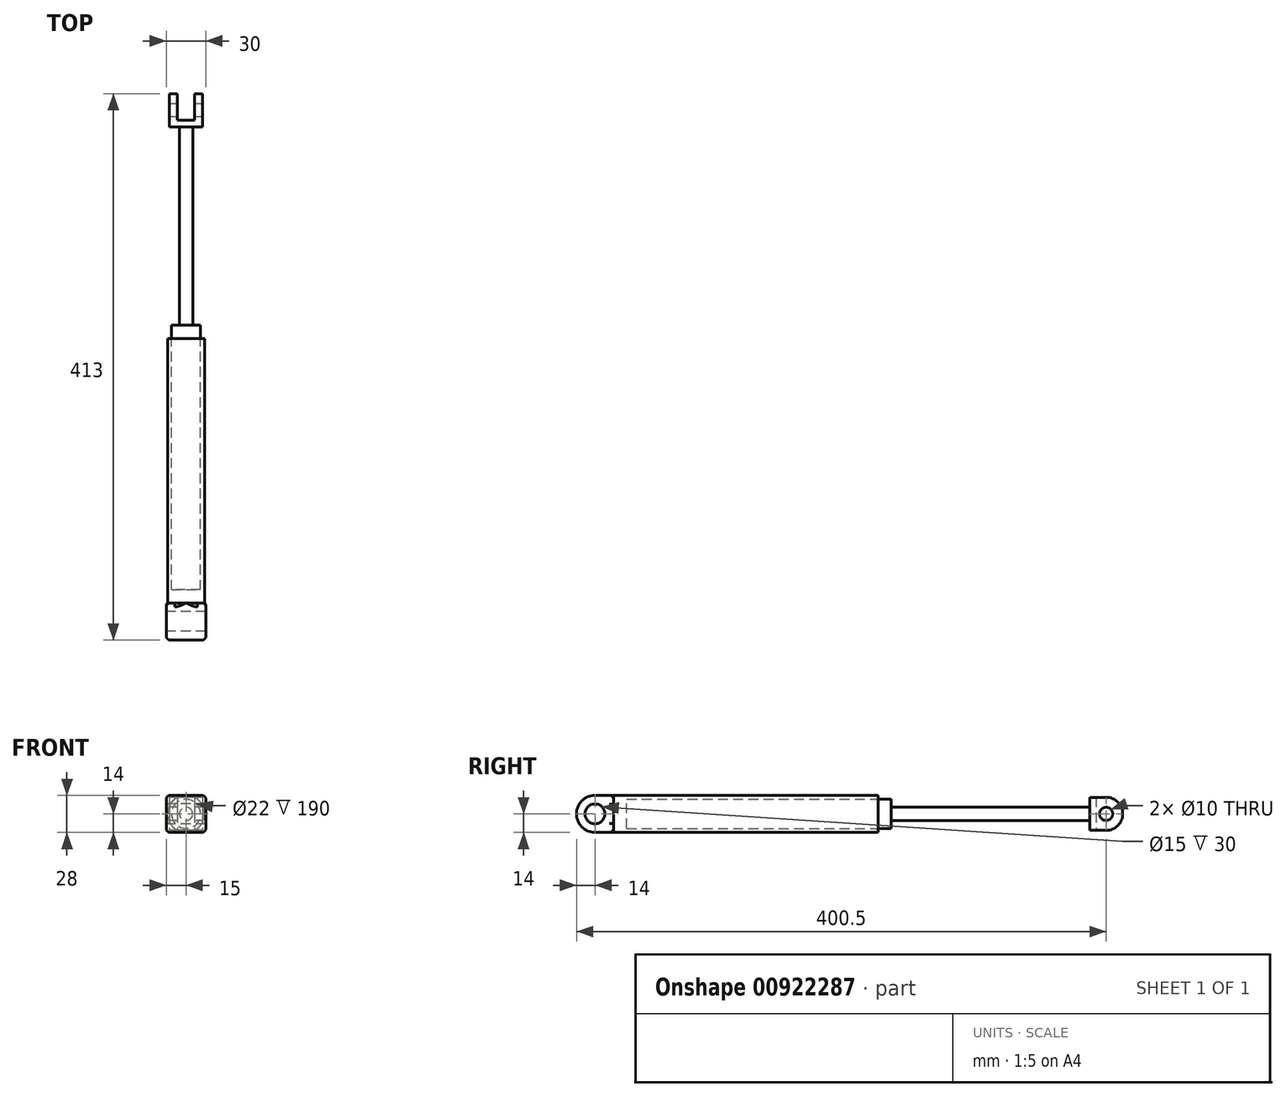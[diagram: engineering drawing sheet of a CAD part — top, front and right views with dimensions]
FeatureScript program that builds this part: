
annotation { "Feature Type Name" : "Feature", "Feature Type Description" : "" }
export const myFeature = defineFeature(function(context is Context, id is Id, definition is map)
    precondition{}
    {
        {
            var Q0;
            Q0=qCreatedBy(makeId("Front.planeOp"),FACE);
            var sketch = newSketch(context, id + "F0", { "sketchPlane" : qUnion([Q0])});
            skCircle(sketch, "E0", {"center": v(0, 0) * mm, "radius": 14 * mm});
            skCircle(sketch, "E1", {"center": v(0, 0) * mm, "radius": 11 * mm});
            skSolve(sketch);
        }
        {
            var Q0;
            Q0=makeQuery(id+"F0.imprint","IMPRINT",FACE,{"disambiguationData":[TD([[makeQuery(id+"F0.imprint","IMPRINT",EDGE,{"derivedFrom":sQuery(id+"F0.wireOp",EDGE,"E0")}),1.0]])]});
            var Q1;
            Q1=makeQuery(id+"F0.imprint","IMPRINT",FACE,{"disambiguationData":[TD([[makeQuery(id+"F0.imprint","IMPRINT",EDGE,{"derivedFrom":sQuery(id+"F0.wireOp",EDGE,"E1")}),1.0]])]});
            extrude(context, id + "F1", {"entities" : qUnion([Q0, Q1]), "depth" : 200 * mm, "offsetDistance" : 25 * mm});
        }
        {
            var Q0;
            Q0=makeQuery(id+"F0.imprint","IMPRINT",FACE,{"disambiguationData":[TD([[makeQuery(id+"F0.imprint","IMPRINT",EDGE,{"derivedFrom":sQuery(id+"F0.wireOp",EDGE,"E1")}),1.0]])]});
            extrude(context, id + "F2", {"entities" : qUnion([Q0]), "operationType" : NewBodyOperationType.REMOVE, "depth" : 190 * mm, "offsetDistance" : 25 * mm});
        }
        {
            var Q0;
            Q0=qCreatedBy(makeId("Right.planeOp"),FACE);
            var sketch = newSketch(context, id + "F3", { "sketchPlane" : qUnion([Q0])});
            skLineSegment(sketch, "E2.bottom", {"start": v(-200, 14) * mm, "end": v(-214, 14) * mm});
            skLineSegment(sketch, "E2.top", {"start": v(-200, -14) * mm, "end": v(-214, -14) * mm});
            skLineSegment(sketch, "E2.left", {"start": v(-200, 14) * mm, "end": v(-200, -14) * mm});
            skLineSegment(sketch, "E2.right", {"start": v(-228, 0) * mm, "end": v(-228, 0) * mm});
            skPoint(sketch, "E3.visualSharp", {"position": v(-228, 14) * mm});
            skArc(sketch, "E3.filletArc", {"start": v(-214, 14) * mm, "mid": v(-223.9, 9.9) * mm, "end": v(-228, 0) * mm});
            skPoint(sketch, "E4.visualSharp", {"position": v(-228, -14) * mm});
            skArc(sketch, "E4.filletArc", {"start": v(-228, 0) * mm, "mid": v(-223.9, -9.9) * mm, "end": v(-214, -14) * mm});
            skCircle(sketch, "E5", {"center": v(-214, 0) * mm, "radius": 7.5 * mm});
            skSolve(sketch);
        }
        {
            var Q0;
            Q0 = qSketchRegion(id + "F3", true);
            extrude(context, id + "F4", {"entities" : qUnion([Q0]), "operationType" : NewBodyOperationType.ADD, "depth" : 30 * mm, "offsetDistance" : 25 * mm, "symmetric" : true});
        }
        {
            var Q0;
            Q0=makeQuery(id+"F4.opExtrude","CAP_EDGE",EDGE,{"disambiguationData":[OSD([sQuery(id+"F3.wireOp",EDGE,"E2.bottom")])],"isStart":true});
            var Q1;
            Q1=makeQuery(id+"F4.opExtrude","CAP_EDGE",EDGE,{"disambiguationData":[OSD([sQuery(id+"F3.wireOp",EDGE,"E2.bottom")])],"isStart":false});
            var Q2;
            Q2=makeQuery(id+"F4.opExtrude","CAP_EDGE",EDGE,{"disambiguationData":[OSD([sQuery(id+"F3.wireOp",EDGE,"E2.left")])],"isStart":false});
            var Q3;
            {var subQ0=sQuery(id+"F3.wireOp",EDGE,"E2.bottom");var subQ1=sQuery(id+"F3.wireOp",EDGE,"E2.left");Q3=makeQuery(id+"F4.boolean.opBoolean","SPLIT",EDGE,{"disambiguationData":[TD([makeQuery(id+"F4.opExtrude","CAP_FACE",FACE,{"disambiguationData":[OSD([subQ0,sQuery(id+"F3.wireOp",EDGE,"E2.top"),subQ1,sQuery(id+"F3.wireOp",EDGE,"E3.filletArc"),sQuery(id+"F3.wireOp",EDGE,"E4.filletArc"),sQuery(id+"F3.wireOp",EDGE,"E5")])],"isStart":false})])],"derivedFrom":makeQuery(id+"F4.opExtrude","SWEPT_EDGE",EDGE,{"disambiguationData":[OSD([subQ0,subQ1])]})});}
            var Q4;
            Q4=makeQuery(id+"F4.opExtrude","CAP_EDGE",EDGE,{"disambiguationData":[OSD([sQuery(id+"F3.wireOp",EDGE,"E2.left")])],"isStart":true});
            var Q5;
            {var subQ0=sQuery(id+"F3.wireOp",EDGE,"E2.left");var subQ1=sQuery(id+"F3.wireOp",EDGE,"E2.top");Q5=makeQuery(id+"F4.boolean.opBoolean","SPLIT",EDGE,{"disambiguationData":[TD([makeQuery(id+"F4.opExtrude","CAP_FACE",FACE,{"disambiguationData":[OSD([sQuery(id+"F3.wireOp",EDGE,"E2.bottom"),subQ1,subQ0,sQuery(id+"F3.wireOp",EDGE,"E3.filletArc"),sQuery(id+"F3.wireOp",EDGE,"E4.filletArc"),sQuery(id+"F3.wireOp",EDGE,"E5")])],"isStart":true})])],"derivedFrom":makeQuery(id+"F4.opExtrude","SWEPT_EDGE",EDGE,{"disambiguationData":[OSD([subQ1,subQ0])]})});}
            fillet(context, id + "F5", {"entities" : qUnion([Q0, Q1, Q2, Q3, Q4, Q5]), "radius" : 3 * mm, "tangentPropagation" : true, "allowEdgeOverflow" : false});
        }
        {
            var Q0;
            Q0=qCreatedBy(makeId("Front.planeOp"),FACE);
            var sketch = newSketch(context, id + "F6", { "sketchPlane" : qUnion([Q0])});
            skCircle(sketch, "E6.0", {"center": v(0, 0) * mm, "radius": 11 * mm});
            skSolve(sketch);
        }
        {
            var Q0;
            Q0 = qSketchRegion(id + "F6", true);
            extrude(context, id + "F7", {"entities" : qUnion([Q0]), "oppositeDirection" : true, "depth" : 10 * mm, "offsetDistance" : 25 * mm});
        }
        {
            var Q0;
            Q0=makeQuery(id+"F7.opExtrude","CAP_FACE",FACE,{"disambiguationData":[OSD([sQuery(id+"F6.wireOp",EDGE,"E6.0")])],"isStart":false});
            var sketch = newSketch(context, id + "F8", { "sketchPlane" : qUnion([Q0])});
            skCircle(sketch, "E7", {"center": v(0, 0) * mm, "radius": 5 * mm});
            skSolve(sketch);
        }
        {
            var Q0;
            Q0 = qSketchRegion(id + "F8", true);
            extrude(context, id + "F9", {"entities" : qUnion([Q0]), "operationType" : NewBodyOperationType.ADD, "depth" : 150 * mm, "offsetDistance" : 25 * mm});
        }
        {
            var Q0;
            Q0=makeQuery(id+"F9.opExtrude","CAP_FACE",FACE,{"disambiguationData":[OSD([sQuery(id+"F8.wireOp",EDGE,"E7")])],"isStart":false});
            var sketch = newSketch(context, id + "F10", { "sketchPlane" : qUnion([Q0])});
            skLineSegment(sketch, "E8.bottom", {"start": v(-12.5, 12.5) * mm, "end": v(12.5, 12.5) * mm});
            skLineSegment(sketch, "E8.top", {"start": v(-12.5, -12.5) * mm, "end": v(12.5, -12.5) * mm});
            skLineSegment(sketch, "E8.left", {"start": v(-12.5, 12.5) * mm, "end": v(-12.5, -12.5) * mm});
            skLineSegment(sketch, "E8.right", {"start": v(12.5, 12.5) * mm, "end": v(12.5, -12.5) * mm});
            skSolve(sketch);
        }
        {
            var Q0;
            Q0 = qSketchRegion(id + "F10", true);
            extrude(context, id + "F11", {"entities" : qUnion([Q0]), "operationType" : NewBodyOperationType.ADD, "depth" : 25 * mm, "offsetDistance" : 25 * mm});
        }
        {
            var Q0;
            Q0=makeQuery(id+"F11.opExtrude","CAP_EDGE",EDGE,{"disambiguationData":[OSD([sQuery(id+"F10.wireOp",EDGE,"E8.bottom")])],"isStart":false});
            var Q1;
            Q1=makeQuery(id+"F11.opExtrude","CAP_EDGE",EDGE,{"disambiguationData":[OSD([sQuery(id+"F10.wireOp",EDGE,"E8.top")])],"isStart":false});
            fillet(context, id + "F12", {"entities" : qUnion([Q0, Q1]), "radius" : 12.5 * mm, "tangentPropagation" : true, "allowEdgeOverflow" : false});
        }
        {
            var Q0;
            Q0=makeQuery(id+"F11.opExtrude","SWEPT_FACE",FACE,{"disambiguationData":[OSD([sQuery(id+"F10.wireOp",EDGE,"E8.right")])]});
            var sketch = newSketch(context, id + "F13", { "sketchPlane" : qUnion([Q0])});
            skCircle(sketch, "E9", {"center": v(-172.5, 0) * mm, "radius": 5 * mm});
            skSolve(sketch);
        }
        {
            var Q0;
            Q0 = qSketchRegion(id + "F13", true);
            extrude(context, id + "F14", {"entities" : qUnion([Q0]), "operationType" : NewBodyOperationType.REMOVE, "endBound" : BoundingType.THROUGH_ALL, "oppositeDirection" : true, "depth" : 25 * mm, "offsetDistance" : 25 * mm});
        }
        {
            var Q0;
            Q0=makeQuery(id+"F11.opExtrude","CAP_FACE",FACE,{"disambiguationData":[OSD([sQuery(id+"F10.wireOp",EDGE,"E8.bottom"),sQuery(id+"F10.wireOp",EDGE,"E8.top"),sQuery(id+"F10.wireOp",EDGE,"E8.left"),sQuery(id+"F10.wireOp",EDGE,"E8.right")])],"isStart":true});
            cPlane(context, id + "F15", {"entities" : qUnion([Q0]), "cplaneType" : CPlaneType.OFFSET, "offset" : 5 * mm, "oppositeDirection" : true, "width" : 150 * mm, "height" : 150 * mm});
        }
        {
            var Q0;
            Q0=qCreatedBy(id+"F15.planeOp",FACE);
            var sketch = newSketch(context, id + "F16", { "sketchPlane" : qUnion([Q0])});
            skLineSegment(sketch, "E10.bottom", {"start": v(6.5, 12.5) * mm, "end": v(-6.5, 12.5) * mm});
            skLineSegment(sketch, "E10.top", {"start": v(6.5, -12.5) * mm, "end": v(-6.5, -12.5) * mm});
            skLineSegment(sketch, "E10.left", {"start": v(6.5, 12.5) * mm, "end": v(6.5, -12.5) * mm});
            skLineSegment(sketch, "E10.right", {"start": v(-6.5, 12.5) * mm, "end": v(-6.5, -12.5) * mm});
            skSolve(sketch);
        }
        {
            var Q0;
            Q0 = qSketchRegion(id + "F16", true);
            extrude(context, id + "F17", {"entities" : qUnion([Q0]), "operationType" : NewBodyOperationType.REMOVE, "endBound" : BoundingType.THROUGH_ALL, "oppositeDirection" : true, "depth" : 25 * mm, "offsetDistance" : 25 * mm});
        }
    });
